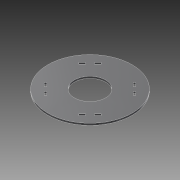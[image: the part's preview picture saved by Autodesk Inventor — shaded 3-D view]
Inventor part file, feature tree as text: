
AUTODESK INVENTOR PART (.ipt)
format: ipt  version: 2021.3 (Build 253353000, 353)  size: 143,872 bytes
history: native  units: mm
features: extrude x3, sketch x3, other x1, pattern_circular x1
ambient origin geometry x8: Origin, YZ Plane, XZ Plane, XY Plane, X Axis, Y Axis, Z Axis, Center Point
bodies: Body1 (feature_tree)
feature tree (8):
  other  "Твердое тело1"
  extrude  "Выдавливание1"  Depth=270.0mm
  extrude  "Выдавливание2"  Depth=6.0mm TaperAngle=0.0deg
  extrude  "Выдавливание3"  Depth=100.0mm
  pattern_circular  "Круговой массив2"  [2 undecoded]
  sketch  "Эскиз1"
  sketch  "Эскиз3"
  sketch  "Эскиз4"
note: 2 required parameter values undecoded (feature->parameter linkage not recoverable at this tier; creation-order binding heuristic only, values carry confidence <= 0.55)
